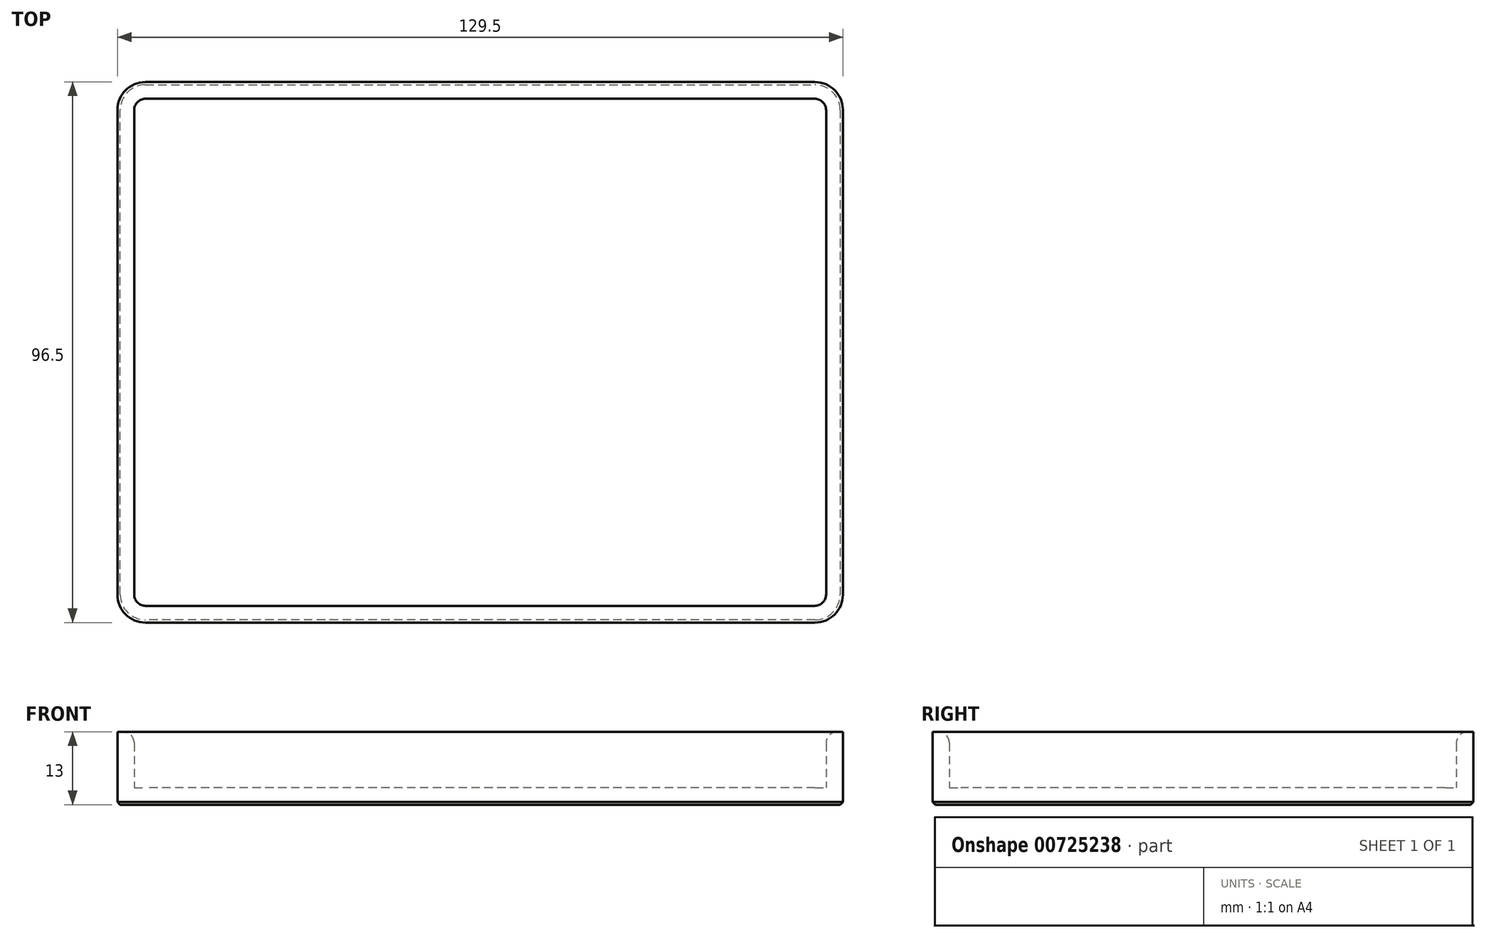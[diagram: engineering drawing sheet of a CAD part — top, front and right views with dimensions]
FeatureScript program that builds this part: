
annotation { "Feature Type Name" : "Feature", "Feature Type Description" : "" }
export const myFeature = defineFeature(function(context is Context, id is Id, definition is map)
    precondition{}
    {
        {
            var Q0;
            Q0=qCreatedBy(makeId("Top.planeOp"),FACE);
            var sketch = newSketch(context, id + "F0", { "sketchPlane" : qUnion([Q0])});
            skLineSegment(sketch, "E0.bottom", {"start": v(0, -15.31) * mm, "end": v(-123.5, -15.31) * mm});
            skLineSegment(sketch, "E0.top", {"start": v(0, -105.81) * mm, "end": v(-123.5, -105.81) * mm});
            skLineSegment(sketch, "E0.left", {"start": v(0, -15.31) * mm, "end": v(0, -105.81) * mm});
            skLineSegment(sketch, "E0.right", {"start": v(-123.5, -15.31) * mm, "end": v(-123.5, -105.81) * mm});
            skLineSegment(sketch, "E1.bottom", {"start": v(-126.5, -12.31) * mm, "end": v(3, -12.31) * mm});
            skLineSegment(sketch, "E1.top", {"start": v(-126.5, -108.81) * mm, "end": v(3, -108.81) * mm});
            skLineSegment(sketch, "E1.left", {"start": v(-126.5, -12.31) * mm, "end": v(-126.5, -108.81) * mm});
            skLineSegment(sketch, "E1.right", {"start": v(3, -12.31) * mm, "end": v(3, -108.81) * mm});
            skSolve(sketch);
        }
        {
            var Q0;
            Q0=makeQuery(id+"F0.imprint","IMPRINT",FACE,{"disambiguationData":[TD([[makeQuery(id+"F0.imprint","IMPRINT",EDGE,{"derivedFrom":sQuery(id+"F0.wireOp",EDGE,"E0.bottom")}),-1.0]])]});
            extrude(context, id + "F1", {"entities" : qUnion([Q0]), "depth" : 10 * mm, "offsetDistance" : 25 * mm});
        }
        {
            var Q0;
            Q0=makeQuery(id+"F1.opExtrude","SWEPT_EDGE",EDGE,{"disambiguationData":[OSD([sQuery(id+"F0.wireOp",EDGE,"E0.top"),sQuery(id+"F0.wireOp",EDGE,"E0.right")])]});
            var Q1;
            Q1=makeQuery(id+"F1.opExtrude","CAP_EDGE",EDGE,{"disambiguationData":[OSD([sQuery(id+"F0.wireOp",EDGE,"E0.top")])],"isStart":false});
            var Q2;
            Q2=makeQuery(id+"F1.opExtrude","CAP_EDGE",EDGE,{"disambiguationData":[OSD([sQuery(id+"F0.wireOp",EDGE,"E0.bottom")])],"isStart":false});
            var Q3;
            Q3=makeQuery(id+"F1.opExtrude","CAP_EDGE",EDGE,{"disambiguationData":[OSD([sQuery(id+"F0.wireOp",EDGE,"E0.right")])],"isStart":false});
            var Q4;
            Q4=makeQuery(id+"F1.opExtrude","SWEPT_EDGE",EDGE,{"disambiguationData":[OSD([sQuery(id+"F0.wireOp",EDGE,"E0.bottom"),sQuery(id+"F0.wireOp",EDGE,"E0.left")])]});
            var Q5;
            Q5=makeQuery(id+"F1.opExtrude","CAP_EDGE",EDGE,{"disambiguationData":[OSD([sQuery(id+"F0.wireOp",EDGE,"E0.left")])],"isStart":false});
            var Q6;
            Q6=makeQuery(id+"F1.opExtrude","SWEPT_EDGE",EDGE,{"disambiguationData":[OSD([sQuery(id+"F0.wireOp",EDGE,"E0.top"),sQuery(id+"F0.wireOp",EDGE,"E0.left")])]});
            var Q7;
            Q7=makeQuery(id+"F1.opExtrude","SWEPT_EDGE",EDGE,{"disambiguationData":[OSD([sQuery(id+"F0.wireOp",EDGE,"E0.bottom"),sQuery(id+"F0.wireOp",EDGE,"E0.right")])]});
            fillet(context, id + "F2", {"entities" : qUnion([Q0, Q1, Q2, Q3, Q4, Q5, Q6, Q7]), "radius" : 2 * mm, "tangentPropagation" : true, "allowEdgeOverflow" : false});
        }
        {
            var Q0;
            Q0=makeQuery(id+"F1.opExtrude","CAP_FACE",FACE,{"disambiguationData":[OSD([sQuery(id+"F0.wireOp",EDGE,"E0.bottom"),sQuery(id+"F0.wireOp",EDGE,"E0.top"),sQuery(id+"F0.wireOp",EDGE,"E0.left"),sQuery(id+"F0.wireOp",EDGE,"E0.right"),sQuery(id+"F0.wireOp",EDGE,"E1.bottom"),sQuery(id+"F0.wireOp",EDGE,"E1.top"),sQuery(id+"F0.wireOp",EDGE,"E1.left"),sQuery(id+"F0.wireOp",EDGE,"E1.right")])],"isStart":true});
            var sketch = newSketch(context, id + "F3", { "sketchPlane" : qUnion([Q0])});
            skLineSegment(sketch, "E2.bottom", {"start": v(3, 12.31) * mm, "end": v(-126.5, 12.31) * mm});
            skLineSegment(sketch, "E2.top", {"start": v(3, 108.81) * mm, "end": v(-126.5, 108.81) * mm});
            skLineSegment(sketch, "E2.left", {"start": v(3, 12.31) * mm, "end": v(3, 108.81) * mm});
            skLineSegment(sketch, "E2.right", {"start": v(-126.5, 12.31) * mm, "end": v(-126.5, 108.81) * mm});
            skSolve(sketch);
        }
        {
            var Q0;
            Q0 = qSketchRegion(id + "F3", true);
            extrude(context, id + "F4", {"entities" : qUnion([Q0]), "operationType" : NewBodyOperationType.ADD, "depth" : 3 * mm, "offsetDistance" : 25 * mm});
        }
        {
            var Q0;
            Q0=makeQuery(id+"F4.boolean.opBoolean","MERGE",EDGE,{"derivedFrom":[makeQuery(id+"F1.opExtrude","SWEPT_EDGE",EDGE,{"disambiguationData":[OSD([sQuery(id+"F0.wireOp",EDGE,"E1.top"),sQuery(id+"F0.wireOp",EDGE,"E1.left")])]}),makeQuery(id+"F4.opExtrude","SWEPT_EDGE",EDGE,{"disambiguationData":[OSD([sQuery(id+"F3.wireOp",EDGE,"E2.top"),sQuery(id+"F3.wireOp",EDGE,"E2.right")])]})]});
            var Q1;
            Q1=makeQuery(id+"F4.boolean.opBoolean","MERGE",EDGE,{"derivedFrom":[makeQuery(id+"F1.opExtrude","SWEPT_EDGE",EDGE,{"disambiguationData":[OSD([sQuery(id+"F0.wireOp",EDGE,"E1.top"),sQuery(id+"F0.wireOp",EDGE,"E1.right")])]}),makeQuery(id+"F4.opExtrude","SWEPT_EDGE",EDGE,{"disambiguationData":[OSD([sQuery(id+"F3.wireOp",EDGE,"E2.top"),sQuery(id+"F3.wireOp",EDGE,"E2.left")])]})]});
            var Q2;
            Q2=makeQuery(id+"F4.boolean.opBoolean","MERGE",EDGE,{"derivedFrom":[makeQuery(id+"F1.opExtrude","SWEPT_EDGE",EDGE,{"disambiguationData":[OSD([sQuery(id+"F0.wireOp",EDGE,"E1.bottom"),sQuery(id+"F0.wireOp",EDGE,"E1.right")])]}),makeQuery(id+"F4.opExtrude","SWEPT_EDGE",EDGE,{"disambiguationData":[OSD([sQuery(id+"F3.wireOp",EDGE,"E2.bottom"),sQuery(id+"F3.wireOp",EDGE,"E2.left")])]})]});
            var Q3;
            Q3=makeQuery(id+"F4.boolean.opBoolean","MERGE",EDGE,{"derivedFrom":[makeQuery(id+"F1.opExtrude","SWEPT_EDGE",EDGE,{"disambiguationData":[OSD([sQuery(id+"F0.wireOp",EDGE,"E1.bottom"),sQuery(id+"F0.wireOp",EDGE,"E1.left")])]}),makeQuery(id+"F4.opExtrude","SWEPT_EDGE",EDGE,{"disambiguationData":[OSD([sQuery(id+"F3.wireOp",EDGE,"E2.bottom"),sQuery(id+"F3.wireOp",EDGE,"E2.right")])]})]});
            fillet(context, id + "F5", {"entities" : qUnion([Q0, Q1, Q2, Q3]), "radius" : 5 * mm, "tangentPropagation" : true, "allowEdgeOverflow" : false});
        }
        {
            var Q0;
            {var subQ0=sQuery(id+"F3.wireOp",EDGE,"E2.right");var subQ1=sQuery(id+"F3.wireOp",EDGE,"E2.top");Q0=makeQuery(id+"F5.opFillet","BLEND_EDGE",EDGE,{"blendedFrom":[makeQuery(id+"F4.boolean.opBoolean","MERGE",EDGE,{"derivedFrom":[makeQuery(id+"F1.opExtrude","SWEPT_EDGE",EDGE,{"disambiguationData":[OSD([sQuery(id+"F0.wireOp",EDGE,"E1.top"),sQuery(id+"F0.wireOp",EDGE,"E1.left")])]}),makeQuery(id+"F4.opExtrude","SWEPT_EDGE",EDGE,{"disambiguationData":[OSD([subQ1,subQ0])]})]}),makeQuery(id+"F4.opExtrude","CAP_FACE",FACE,{"disambiguationData":[OSD([sQuery(id+"F3.wireOp",EDGE,"E2.bottom"),subQ1,sQuery(id+"F3.wireOp",EDGE,"E2.left"),subQ0])],"isStart":false})],"blendedInto":[makeQuery(id+"F4.opExtrude","CAP_FACE",FACE,{"disambiguationData":[OSD([sQuery(id+"F3.wireOp",EDGE,"E2.bottom"),subQ1,sQuery(id+"F3.wireOp",EDGE,"E2.left"),subQ0])],"isStart":false})]});}
            var Q1;
            Q1=makeQuery(id+"F4.opExtrude","CAP_EDGE",EDGE,{"disambiguationData":[OSD([sQuery(id+"F3.wireOp",EDGE,"E2.top")])],"isStart":false});
            var Q2;
            Q2=makeQuery(id+"F4.opExtrude","CAP_EDGE",EDGE,{"disambiguationData":[OSD([sQuery(id+"F3.wireOp",EDGE,"E2.right")])],"isStart":false});
            var Q3;
            {var subQ0=sQuery(id+"F3.wireOp",EDGE,"E2.left");var subQ1=sQuery(id+"F3.wireOp",EDGE,"E2.top");Q3=makeQuery(id+"F5.opFillet","BLEND_EDGE",EDGE,{"blendedFrom":[makeQuery(id+"F4.boolean.opBoolean","MERGE",EDGE,{"derivedFrom":[makeQuery(id+"F1.opExtrude","SWEPT_EDGE",EDGE,{"disambiguationData":[OSD([sQuery(id+"F0.wireOp",EDGE,"E1.top"),sQuery(id+"F0.wireOp",EDGE,"E1.right")])]}),makeQuery(id+"F4.opExtrude","SWEPT_EDGE",EDGE,{"disambiguationData":[OSD([subQ1,subQ0])]})]}),makeQuery(id+"F4.opExtrude","CAP_FACE",FACE,{"disambiguationData":[OSD([sQuery(id+"F3.wireOp",EDGE,"E2.bottom"),subQ1,subQ0,sQuery(id+"F3.wireOp",EDGE,"E2.right")])],"isStart":false})],"blendedInto":[makeQuery(id+"F4.opExtrude","CAP_FACE",FACE,{"disambiguationData":[OSD([sQuery(id+"F3.wireOp",EDGE,"E2.bottom"),subQ1,subQ0,sQuery(id+"F3.wireOp",EDGE,"E2.right")])],"isStart":false})]});}
            var Q4;
            Q4=makeQuery(id+"F4.opExtrude","CAP_EDGE",EDGE,{"disambiguationData":[OSD([sQuery(id+"F3.wireOp",EDGE,"E2.left")])],"isStart":false});
            var Q5;
            {var subQ0=sQuery(id+"F3.wireOp",EDGE,"E2.right");var subQ1=sQuery(id+"F3.wireOp",EDGE,"E2.bottom");Q5=makeQuery(id+"F5.opFillet","BLEND_EDGE",EDGE,{"blendedFrom":[makeQuery(id+"F4.boolean.opBoolean","MERGE",EDGE,{"derivedFrom":[makeQuery(id+"F1.opExtrude","SWEPT_EDGE",EDGE,{"disambiguationData":[OSD([sQuery(id+"F0.wireOp",EDGE,"E1.bottom"),sQuery(id+"F0.wireOp",EDGE,"E1.left")])]}),makeQuery(id+"F4.opExtrude","SWEPT_EDGE",EDGE,{"disambiguationData":[OSD([subQ1,subQ0])]})]}),makeQuery(id+"F4.opExtrude","CAP_FACE",FACE,{"disambiguationData":[OSD([subQ1,sQuery(id+"F3.wireOp",EDGE,"E2.top"),sQuery(id+"F3.wireOp",EDGE,"E2.left"),subQ0])],"isStart":false})],"blendedInto":[makeQuery(id+"F4.opExtrude","CAP_FACE",FACE,{"disambiguationData":[OSD([subQ1,sQuery(id+"F3.wireOp",EDGE,"E2.top"),sQuery(id+"F3.wireOp",EDGE,"E2.left"),subQ0])],"isStart":false})]});}
            var Q6;
            Q6=makeQuery(id+"F4.opExtrude","CAP_EDGE",EDGE,{"disambiguationData":[OSD([sQuery(id+"F3.wireOp",EDGE,"E2.bottom")])],"isStart":false});
            var Q7;
            {var subQ0=sQuery(id+"F3.wireOp",EDGE,"E2.left");var subQ1=sQuery(id+"F3.wireOp",EDGE,"E2.bottom");Q7=makeQuery(id+"F5.opFillet","BLEND_EDGE",EDGE,{"blendedFrom":[makeQuery(id+"F4.boolean.opBoolean","MERGE",EDGE,{"derivedFrom":[makeQuery(id+"F1.opExtrude","SWEPT_EDGE",EDGE,{"disambiguationData":[OSD([sQuery(id+"F0.wireOp",EDGE,"E1.bottom"),sQuery(id+"F0.wireOp",EDGE,"E1.right")])]}),makeQuery(id+"F4.opExtrude","SWEPT_EDGE",EDGE,{"disambiguationData":[OSD([subQ1,subQ0])]})]}),makeQuery(id+"F4.opExtrude","CAP_FACE",FACE,{"disambiguationData":[OSD([subQ1,sQuery(id+"F3.wireOp",EDGE,"E2.top"),subQ0,sQuery(id+"F3.wireOp",EDGE,"E2.right")])],"isStart":false})],"blendedInto":[makeQuery(id+"F4.opExtrude","CAP_FACE",FACE,{"disambiguationData":[OSD([subQ1,sQuery(id+"F3.wireOp",EDGE,"E2.top"),subQ0,sQuery(id+"F3.wireOp",EDGE,"E2.right")])],"isStart":false})]});}
            chamfer(context, id + "F6", {"entities" : qUnion([Q0, Q1, Q2, Q3, Q4, Q5, Q6, Q7]), "width" : 0.5 * mm, "tangentPropagation" : true});
        }
    });
